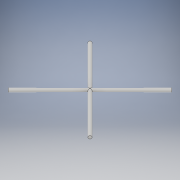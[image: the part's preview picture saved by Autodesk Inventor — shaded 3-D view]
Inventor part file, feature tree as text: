
AUTODESK INVENTOR PART (.ipt)
format: ipt  version: 2018 (Build 220112000, 112)  size: 127,488 bytes
history: native  units: in
note: dims shown in document units (in); Inventor stores cm internally (conversion verified against a paired STEP export)
features: other x9, plane x8, sketch x5, reference x4, extrude x2
ambient origin geometry x8: Origin, YZ Plane, XZ Plane, XY Plane, X Axis, Y Axis, Z Axis, Center Point
bodies: Solid1 (feature_tree)
feature tree (28):
  sketch  "Sketch1"  dims[d0=12.0in d1=6.0in]
  other  "Work Axis1"
  plane  "Work Plane1"
  extrude  "Extrusion1"  Depth=6.0in
  sketch  "Sketch3"  dims[d4=10.2869in]
  sketch  "Sketch4"  dims[d5=138.381in]
  other  "Work Axis2"
  plane  "Work Plane2"
  other  "Work Axis4"
  plane  "Work Plane7"
  plane  "Work Plane8"
  extrude  "Extrusion2"  Depth=62.9988in
  reference  "Reference1"
  reference  "Reference2"
  reference  "Reference3"
  reference  "Reference4"
  sketch  "Sketch2"  dims[d2=125.9977in d3=62.9988in]
  plane  "Work Plane3"
  plane  "Work Plane4"
  other  "Work Axis3"
  plane  "Work Plane5"
  plane  "Work Plane6"
  sketch  "Sketch5"  dims[d6=315.0deg d7=4.0in d8=150.0in d9=0.0in d10=150.0in d11=75.0in d12=45.0deg d13=90.0deg d14=-75.0in d15=315.0deg d16=-75.0in d17=4.0in d18=150.0in d19=0.0in]
  other  "FullRadiusPole_x2_AJB.iam"
  other  "FullRadiusPoleAJB:1"
  other  "1_6RadiusPole_WithBolt_AJB:1"
  other  "1_6RadiusPoleAJB:1"
  other  "1_6RadiusPole_WithBolt_AJB:6"
